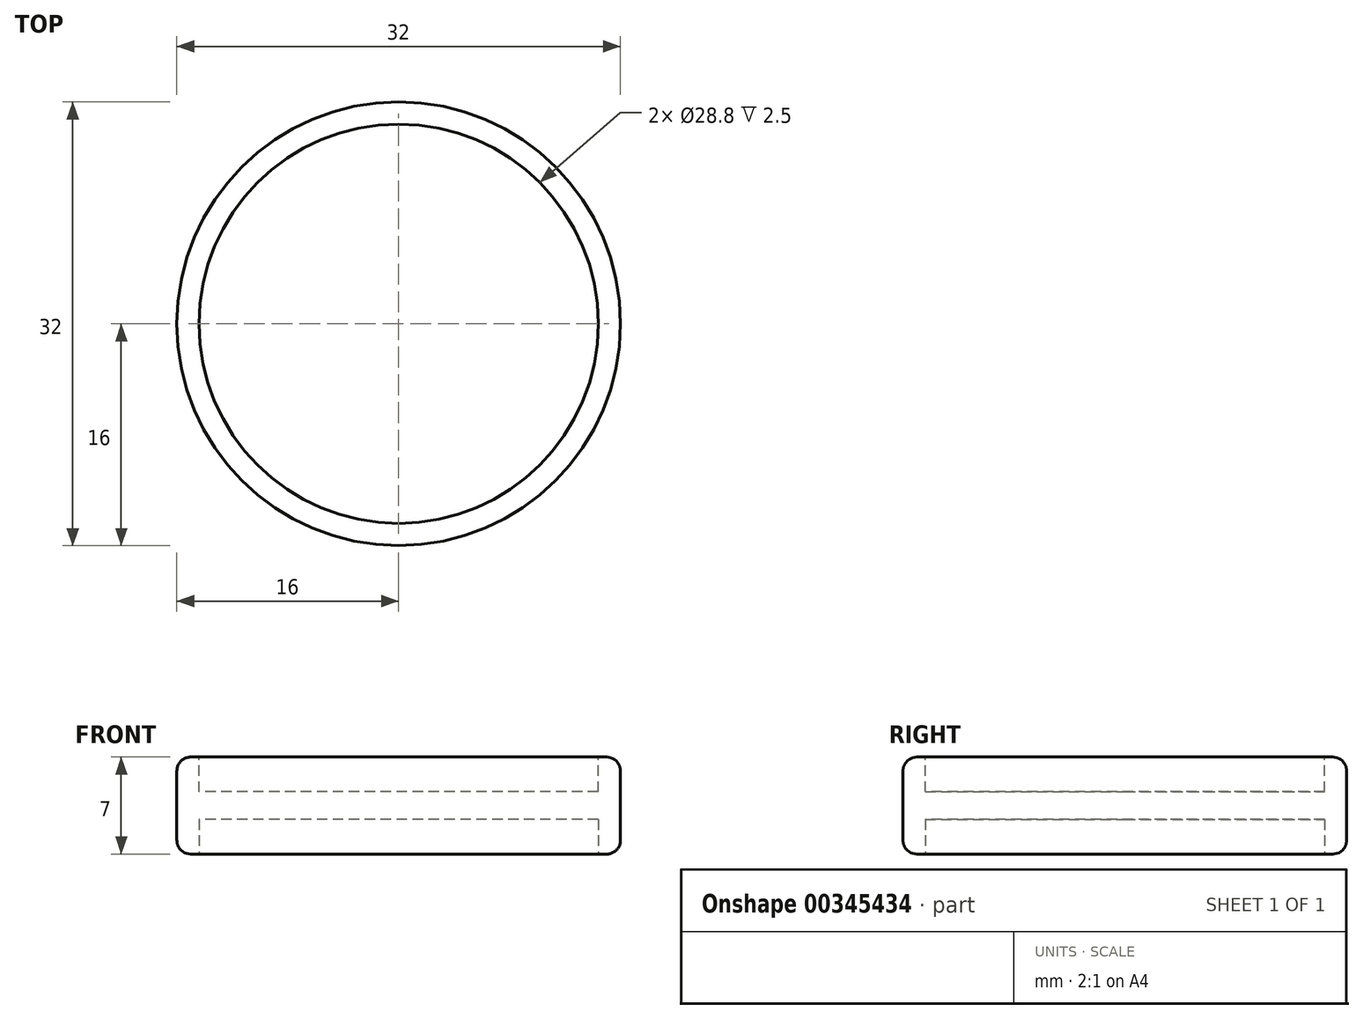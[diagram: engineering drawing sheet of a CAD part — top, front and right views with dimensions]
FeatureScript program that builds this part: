
annotation { "Feature Type Name" : "Feature", "Feature Type Description" : "" }
export const myFeature = defineFeature(function(context is Context, id is Id, definition is map)
    precondition{}
    {
        {
            var Q0;
            Q0=qCreatedBy(makeId("Front.planeOp"),FACE);
            var sketch = newSketch(context, id + "F0", { "sketchPlane" : qUnion([Q0])});
            skLineSegment(sketch, "E0", {"start": v(0, 0) * mm, "end": v(-16, 0) * mm});
            skLineSegment(sketch, "E1", {"start": v(-16, 0) * mm, "end": v(-16, 3.5) * mm});
            skLineSegment(sketch, "E2", {"start": v(-16, 3.5) * mm, "end": v(-14.4, 3.5) * mm});
            skLineSegment(sketch, "E3", {"start": v(-14.4, 3.5) * mm, "end": v(-14.4, 1) * mm});
            skLineSegment(sketch, "E4", {"start": v(-14.4, 1) * mm, "end": v(0, 1) * mm});
            skLineSegment(sketch, "E5", {"start": v(0, 1) * mm, "end": v(0, 0) * mm});
            skLineSegment(sketch, "E6", {"start": v(0, 9.17) * mm, "end": v(0, -11.42) * mm, "construction": true});
            skSolve(sketch);
        }
        {
            var Q0;
            Q0=makeQuery(id+"F0.imprint","IMPRINT",FACE,{"disambiguationData":[TD([[makeQuery(id+"F0.imprint","IMPRINT",EDGE,{"derivedFrom":sQuery(id+"F0.wireOp",EDGE,"E0")}),-1.0]])]});
            var Q1;
            Q1=sQuery(id+"F0.wireOp",EDGE,"E6");
            revolve(context, id + "F1", {"entities" : qUnion([Q0]), "axis" : qUnion([Q1]), "revolveType" : RevolveType.FULL});
        }
        {
            var Q0;
            Q0=makeQuery(id+"F1.opRevolve","SWEPT_BODY",BODY,{"disambiguationData":[OSD([sQuery(id+"F0.wireOp",EDGE,"E0"),sQuery(id+"F0.wireOp",EDGE,"E1"),sQuery(id+"F0.wireOp",EDGE,"E2"),sQuery(id+"F0.wireOp",EDGE,"E3"),sQuery(id+"F0.wireOp",EDGE,"E4"),sQuery(id+"F0.wireOp",EDGE,"E5")])]});
            var Q1;
            Q1=qCreatedBy(makeId("Top.planeOp"),FACE);
            mirror(context, id + "F2", {"operationType" : NewBodyOperationType.ADD, "entities" : qUnion([Q0]), "mirrorPlane" : qUnion([Q1])});
        }
        {
            var Q0;
            Q0=makeQuery(id+"F1.opRevolve","SWEPT_EDGE",EDGE,{"disambiguationData":[OSD([sQuery(id+"F0.wireOp",EDGE,"E1"),sQuery(id+"F0.wireOp",EDGE,"E2")])]});
            fillet(context, id + "F3", {"entities" : qUnion([Q0]), "radius" : 1 * mm, "tangentPropagation" : true, "allowEdgeOverflow" : false});
        }
        {
            var Q0;
            Q0=makeQuery(id+"F2.opPattern","COPY",EDGE,{"derivedFrom":makeQuery(id+"F1.opRevolve","SWEPT_EDGE",EDGE,{"disambiguationData":[OSD([sQuery(id+"F0.wireOp",EDGE,"E1"),sQuery(id+"F0.wireOp",EDGE,"E2")])]}),"instanceName":"1"});
            fillet(context, id + "F4", {"entities" : qUnion([Q0]), "radius" : 1 * mm, "tangentPropagation" : true, "allowEdgeOverflow" : false});
        }
    });
